# Revit family: IS_Tempo_BIM_GB
name_source: partatom
category: Casework
units: mm (PartAtom-declared; Revit-internal decimal feet)

## family parameters
Cut with Voids When Loaded = No
Host = Face
OmniClass Number = 23.40.35.00
OmniClass Title = Casework
Room Calculation Point = No
Shared = Yes

## types (1)
- E0777WG - Tempo 650 mm WC unit with adjustable cistern - White gloss
    Accessories = www.idealspec.co.uk
    AreaUnits = millimeters
    Assembly Code = C1030200
    AssetType = Fixed
    BIMObjectName = ISI_IdealStandard_BathroomIntegratedFurniture_Tempo_E0777WG
    BIMobject category = Basins
    Brand = Ideal Standard
    CodePerformance = FSC, EN 14749:2005
    Color = Sandy Grey
    ConnectionType = Mechanical
    Cost = 0 $
    Default Elevation = 830 mm  [stored 2.7231 ft]
    Depth = 300 mm
    Description = Tempo 650 mm wc unit with adjustable cistern for 6/4 or 4/2.6 litre flush
4/2.6 litre flush
    DurationUnit = year
    EAN code = https://#N
    Edition number = 1
    ExpectedLife = 30
    Features = Adjustable cistern and push button
    Finish = Sandy Grey
    Height = 830 mm  [stored 2.7231 ft]
    IFC Classification = Sanitary Terminal
    IfcExportAs = IfcFurnitureType
    IfcExportType = Bathroom integrated furniture
    InstallationInstructions = www.idealspec.co.uk/resources.html
    LaminateMtl = ISI_IdealStandard_Laminate_WhiteGloss_Render
    LinearUnits = millimeters
    MainColor = Sandy Grey
    Manufacturer name = Ideal Standard
    ManufacturerURL = www.idealspec.co.uk
    Material = Varies, see product information
    MetalMtl = ISI_IdealStandard_Handles_Silver_Render
    Model = E0777WG
    ModelNumber = E0777WG
    ModelReference = Tempo 650 mm wc unit with adjustable cistern for 6/4 or 4/2.6 litre flush
4/2.6 litre flush
    NBS Reference Code = 35-75-08
    NBS Reference Description = Bathroom Cabinets
    Name = BathroomIntegratedFurniture_Tempo_E0777WG_IdealStandard
    Nominal height = 830
    Nominal width = 650
    NominalDepth = 300 mm
    NominalLength = 300 mm
    OmniClass Code = 23-31 17 11
    OmniClass Description = Shower Compartments
    Product Guid = 464d868d-be48-406c-b4b0-7bbd169b40b0
    Product SKU = E0777
    Product data url = https://bimobject.com
    Product family = Sanitary
    Product group = Bathroom integrated furniture
    ProductInformation = www.idealspec.co.uk/assets/datasheet/E0777WG
    QR code = http://bimobject.com
    Shape = Rectangular
    Size = 830 x 650 x 300 mm
    Space = Internal
    SpareParts = www.fastpart-spares.co.uk
    Style = Bathroom cupboards
    SustainabilityPerformance = FSC
    Technical description = https://www.idealspec.co.uk
    URL = www.idealspec.co.uk
    Uniclass 2.0 Code = PR-35-75-08
    Uniclass 2.0 Description = Bathroom Cabinets
    Uniclass 2015 Code = Pr_40_30_78_04
    Uniclass 2015 Name = Bathroom cupboards
    Version = 2
    VolumeUnits = Litres
    WarrantyDescription = Manufacturers warranty
    WarrantyDurationParts = 5
    WarrantyDurationUnit = year
    Weight Net (Kg) = 0
    Width = 650 mm  [stored 2.13255 ft]

note: [stored X ft] marks values corroborated as IEEE doubles in the binary element streams (Revit-internal decimal feet)

## geometry (parser evidence)
native form markers: Blend x6, Sweep x1
no freeform markers — native parametric forms only
